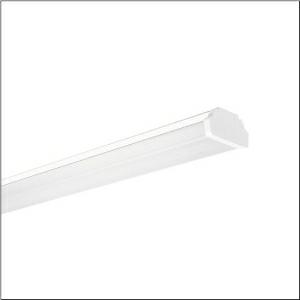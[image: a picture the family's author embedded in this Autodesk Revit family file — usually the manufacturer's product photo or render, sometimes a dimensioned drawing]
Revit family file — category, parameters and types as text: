
# Revit family: dus_31_gen_2_53bd812mv4cxd2_7e42
name_source: partatom
category: Lighting Fixtures
units: mm (PartAtom-declared; Revit-internal decimal feet)

## family parameters
Cut with Voids When Loaded = No
Host = Face
Light Source = No
Part Type = Normal
Room Calculation Point = No
Round Connector Dimension = Use Diameter
Shared = No

## types (1)
- --- (1 x LED, 12350 lm, 64.6 W, 4000K)
    Apparent Load = 65 VA
    CIE Flux Codes = 47 80 95 93 100
    Color Rendering = 80
    Color Temperature = 4000K
    Default Elevation = 1800 mm
    Description = DUS 31 Gen.2, luminaire insert, of sheet steel, coil coated, white, length: 1.535mm, width: 81mm, height: 90mm, 5x system unit, system units: 307mm, LED rated luminous flux: 12.350lm, light colour: 840, SDCM (Standard Deviation of Colour Matching)MacAdam ≤ 3 SDCM (initial), control gear: ON/OFF Multilumen, control gear: ECG, with plug, 3-pole, with phase selection, mains connection: 220..240V, AC, 50/60Hz, rated input power: 65W, through-wiring accessed according to module size, primary optical cover: cover, of PMMA, light emission: direct distribution, primary light characteristic: symmetric, protection rating (complete): IP20, protection rating (LED compartment): IP50, insulation class (complete): insulation class I (protective earthing), certification: CE, ENEC, VDE, UKCA, impact resistance: IK03, permissible ambient temperature for indoor applications: -35..+40°C, corresponds to IFS (International Featured Standards) requirements for safety and quality in the food industry, reducing of maximum allowable ambient temperature of 5°C with ceiling mounting, packaging unit: 1 piece
    Height = 95 mm
    Lamp = 1 x LED
    Lamp Light Flux = 12350 lm
    Lamp Power = 64.6 W
    Lamp count = 1
    Length = 1535 mm
    Luminous efficacy = 191 lm/W
    Manufacturer = Siteco
    ModVariant = No
    Model = 53BD812MV4CXD2
    Mounting Place = Ceiling
    Mounting Type = Pendant
    Number of Poles = 1
    OnlyDefault = Yes
    Power Factor = 1
    Product Name = DUS 31 Gen.2
    Product group = luminaire insert | ceiling pendant
    ProductGroupID = 901
    Protection Class = Protection class I
    Protection Degree = IP 20
    RLX_Detail_Level = 1
    RLX_Emergency_Light_Flux = 0 lm
    RLX_Emergency_Type = 0
    RLX_Emergency_Type_DB = No
    RlxData = <blob elided: 29945 chars, md5=84b63139>
    Socket = socket
    Standby Power = 0 W
    System Light Flux = 12350 lm
    System Power = 65 W
    Type Comments = factory setting: luminous flux: 100 % | (A | C | E) | 152 mA
    Type Image = l_1319596.jpg
    URL = http://relux.com
    VarID = @adj_040835
    Voltage = 0 V
    Weight = 0.00 kg
    Width = 81 mm

## geometry (parser evidence)
native form markers: Blend x4, Sweep x15
no freeform markers — native parametric forms only
